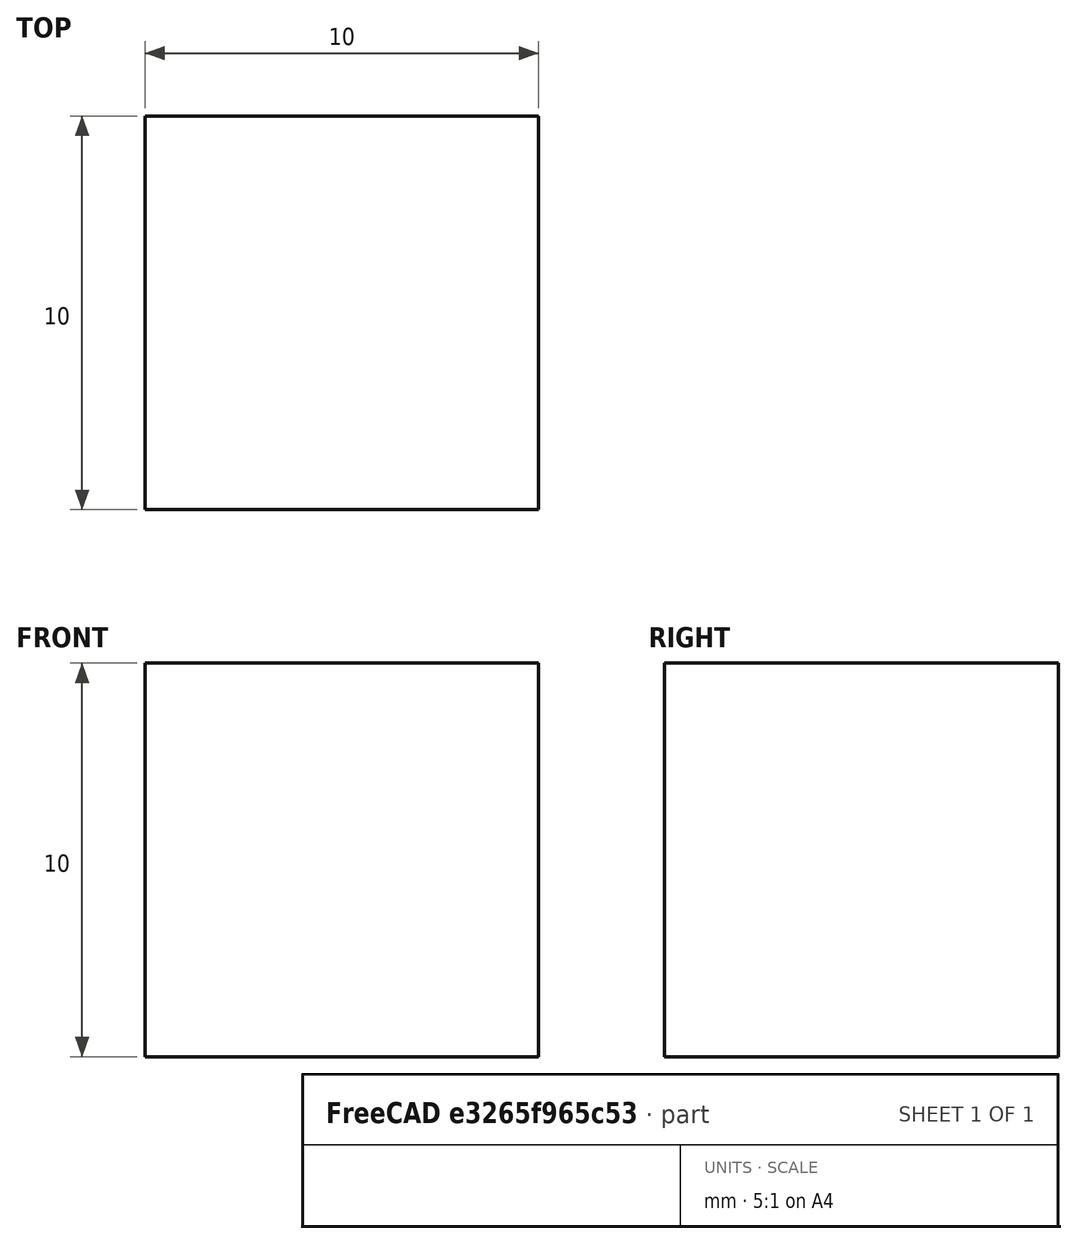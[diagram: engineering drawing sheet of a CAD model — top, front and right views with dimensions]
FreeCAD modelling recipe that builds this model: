
FCSTD DOCUMENT  (FreeCAD 1.0R39109 (Git))
Label: box
License: All rights reserved
LicenseURL: http://en.wikipedia.org/wiki/All_rights_reserved
objects: Part::Plane×4, Part::FeaturePython×1, Fem::ConstraintFixed×1, Fem::ConstraintForce×1, Fem::FemMeshShapeBaseObjectPython×1, Fem::FemSolverObjectPython×1, Fem::FeaturePython×1, App::MaterialObjectPython×1, Fem::FemMeshObjectPython×1, Fem::FemResultObjectPython×1, Fem::FemPostPipeline×1, App::TextDocument×1, Fem::FemAnalysis×1
note: 5 computed .brp shape members not serialized (recipe doc carries the construction recipe); baked Part::Feature solids carry a one-line shape summary decoded from their .brp

FEATURE [Part::Plane] Plane
  AttacherType = Attacher::AttachEngine3D
  Length = 10
  Placement = pos=(0,0,-10) rot=(0,0,1;0rad)
  Width = 10
FEATURE [Part::Plane] Plane001
  AttacherType = Attacher::AttachEngine3D
  Length = 10
  Placement = pos=(0,0,0) rot=(0,1,0;1.5708rad)
  Width = 10
FEATURE [Part::Plane] Plane002
  AttacherType = Attacher::AttachEngine3D
  Length = 10
  Placement = pos=(10,0,0) rot=(0,1,0;1.5708rad)
  Width = 10
FEATURE [Part::Plane] Plane003
  AttacherType = Attacher::AttachEngine3D
  Length = 10
  Width = 10
FEATURE [Part::FeaturePython] BooleanFragments  # WARN: FeaturePython — macro-defined, semantics opaque (R4)
  Mode = 0
  Objects = -> [Plane,Plane001,Plane002,Plane003]
  Tolerance = 0
FEATURE [Fem::ConstraintFixed] ConstraintFixed
  NormalDirection = (0,0,1)
  Normals = (4) [(0,0,1),(0,0,1),(0,0,1),(0,0,1)]
  Points = (4) [(0,0,-10),(0,10,-10),(10,0,-10),(10,10,-10)]
  References = -> [BooleanFragments]
  Suppressed = false
FEATURE [Fem::ConstraintForce] ConstraintForce
  Direction = -> BooleanFragments [Edge11]
  DirectionVector = (1,0,0)
  Force = 1000
  NormalDirection = (0,0,1)
  Normals = (2) [(0,0,1),(0,0,1)]
  Points = (2) [(0,0,0),(0,10,0)]
  References = -> [BooleanFragments]
  Suppressed = false
FEATURE [Fem::FemMeshShapeBaseObjectPython] FEMMeshGmsh  # FEM object (typed FeaturePython)
  Algorithm2D = 0
  Algorithm3D = 0
  CharacteristicLengthMax = 0
  CharacteristicLengthMin = 0
  CoherenceMesh = true
  ElementDimension = 2
  ElementOrder = 1
  GeometryTolerance = 1e-06
  GroupsOfNodes = false
  HighOrderOptimize = 0
  MeshSizeFromCurvature = 12
  OptimizeNetgen = false
  OptimizeStd = true
  RecombinationAlgorithm = 0
  Recombine3DAll = false
  RecombineAll = false
  SecondOrderLinear = false
  Shape = -> BooleanFragments
  SubdivisionAlgorithm = 0
FEATURE [Fem::FemSolverObjectPython] SolverCcxTools  # FEM object (typed FeaturePython)
  AnalysisType = 0
  BeamReducedIntegration = true
  BeamShellResultOutput3D = false
  BucklingFactors = 1
  EigenmodeHighLimit = 1000000
  EigenmodeLowLimit = 0
  EigenmodesCount = 10
  GeometricalNonlinearity = 0
  IterationsControlParameterCutb = 0.25,0.5,0.75,0.85,,,1.5,
  IterationsControlParameterIter = 4,8,9,200,10,400,,200,,
  IterationsControlParameterTimeUse = false
  IterationsMaximum = 2000
  IterationsUserDefinedIncrementations = false
  IterationsUserDefinedTimeStepLength = false
  MaterialNonlinearity = 0
  MatrixSolverType = 0
  ModelSpace = 0
  OutputFrequency = 1
  SplitInputWriter = false
  ThermoMechSteadyState = true
  ThermoMechType = 0
  TimeEnd = 1
  TimeInitialStep = 0.01
  TimeMaximumStep = 1
  TimeMinimumStep = 1e-05
FEATURE [Fem::FeaturePython] ElementGeometry2D  # FEM object (typed FeaturePython)
  Thickness = 1
FEATURE [App::MaterialObjectPython] MaterialSolid  # material (typed FeaturePython)
  Category = 0
  Material = AmbientColor=(0.0020, 0.0020, 0.0020, 1.0),Author=Juergen Riegel,AuthorAndLicense=CC-BY-3.0,CardName=CalculiX-Steel,Density=7.9e-06 kg/mm^3,+14 more (map truncated)
  UUID = 92589471-a6cb-4bbc-b748-d425a17dea7d
FEATURE [Fem::FemMeshObjectPython] CCX_Results_Mesh  # FEM object (typed FeaturePython)
FEATURE [Fem::FemResultObjectPython] CCX_Results  # FEM object (typed FeaturePython)
  DisplacementLengths = [0,0,0,0,0.000317151,0.000317149,0.00031497,0.000314968,0,0,0,0,0,0,0,0,0,0,0,2.94628e-09,3.02415e-09,3.00043e-09,3.02909e-09,2.95756e-09,3.97421e-09,3.19864e-09,3.05178e-09,3.05413e-09,3.20728e-09,3.98628e-09,0,0,0,0,0,0,0,0,0,0,0,+839 more]
  DisplacementVectors = (880) [(0,0,0),(0,0,0),(0,0,0),(0,0,0),(0.00031715,-8.45803e-07,3.88839e-07),(0.000317148,8.44059e-07,3.89458e-07),(0.000314969,4.78234e-07,-6.08826e-07),+873 more]
  Eigenmode = 0
  EigenmodeFrequency = 0
  MaxShear = [0.0548959,0.0548447,0.0544567,0.0544046,0.0746887,0.0747767,0.0625416,0.0625647,0.0440682,0.0337027,0.0362306,0.0337779,0.0440447,0.0182881,0.0370169,0.0377786,0.0379453,0.0370668,0.0182972,0.000184373,3.73367e-05,1.79001e-06,3.76396e-05,+857 more]
  Mesh = -> CCX_Results_Mesh
  NodeNumbers = [1,2,3,4,5,6,7,8,9,10,11,12,13,14,15,16,17,18,19,20,21,22,23,24,25,26,27,28,29,30,31,32,33,34,35,36,37,38,39,40,41,42,43,44,45,46,47,48,49,50,51,52,53,54,55,56,57,58,59,60,61,62,63,64,65,66,67,68,69,+811 more]
  NodeStrainXX = [-2.93483e-08,-2.93743e-08,2.93671e-08,2.93902e-08,-3.64062e-07,-3.64326e-07,1.67714e-07,1.67519e-07,-2.30956e-08,-2.23958e-08,-2.639e-08,-2.24236e-08,-2.31302e-08,-2.04316e-08,-1.74632e-08,-2.17632e-08,-2.18188e-08,-1.74988e-08,+862 more]
  NodeStrainXY = [-3.77972e-08,3.7876e-08,-3.76633e-08,3.77454e-08,1.46119e-07,-1.46048e-07,1.58126e-07,-1.58018e-07,-1.56336e-08,-1.47411e-08,-1.19399e-10,1.42119e-08,1.57255e-08,-3.05797e-08,-1.99003e-09,-1.67503e-08,1.65514e-08,1.988e-09,3.06329e-08,+861 more]
  NodeStrainXZ = [-3.28965e-07,-3.28617e-07,-3.26214e-07,-3.25861e-07,-1.93783e-07,-1.94471e-07,-1.91882e-07,-1.92055e-07,2.67141e-07,2.02304e-07,2.18259e-07,2.02819e-07,2.66978e-07,9.20066e-08,2.24644e-07,2.28393e-07,2.29457e-07,2.2495e-07,9.20384e-08,+861 more]
  NodeStrainYY = [-1.48238e-08,-1.48194e-08,1.46836e-08,1.46785e-08,3.32011e-07,3.32288e-07,-2.59411e-07,-2.59437e-07,5.98466e-10,2.66905e-11,-3.22278e-10,2.27532e-11,5.99342e-10,8.69394e-14,5.33533e-14,9.81687e-14,9.9542e-14,5.36697e-14,8.69007e-14,+861 more]
  NodeStrainYZ = [3.4744e-08,-3.47794e-08,-3.43382e-08,3.43731e-08,-1.74433e-07,1.74363e-07,1.60923e-07,-1.60994e-07,2.196e-08,1.08085e-08,-9.82232e-12,-1.08047e-08,-2.19582e-08,2.88637e-08,1.57787e-08,5.55385e-09,-5.55607e-09,-1.57829e-08,-2.88644e-08,+861 more]
  NodeStrainZZ = [1.12252e-07,1.12324e-07,-1.12152e-07,-1.12216e-07,-1.85121e-07,-1.85344e-07,2.12696e-07,2.12981e-07,7.22729e-08,7.19567e-08,7.68914e-08,7.19965e-08,7.23315e-08,7.60434e-08,6.7106e-08,7.18585e-08,7.18882e-08,6.71643e-08,7.60949e-08,+861 more]
  NodeStressXX = [0.00350727,0.00350917,-0.00350683,-0.0035087,-0.0851212,-0.0851893,0.0417518,0.0417281,0.00229968,0.00238994,0.00181638,0.00238643,0.00229711,0.0034371,0.00319343,0.00255365,0.00254155,0.00319045,0.00343942,-1.44183e-05,5.30419e-06,+859 more]
  NodeStressXY = [-0.0061057,0.00611843,-0.00608407,0.00609734,0.0236038,-0.0235924,0.0255433,-0.0255259,-0.00252542,-0.00238125,-1.92876e-05,0.00229577,0.00254027,-0.0049398,-0.000321466,-0.00270581,0.00267368,0.000321139,0.00494839,3.88318e-05,1.16268e-05,+859 more]
  NodeStressXZ = [-0.0531406,-0.0530843,-0.0526962,-0.0526391,-0.0313033,-0.0314146,-0.0309964,-0.0310242,0.0431536,0.0326799,0.0352572,0.032763,0.0431273,0.0148626,0.0362887,0.0368943,0.0370661,0.0363381,0.0148677,-1.79571e-18,-3.50672e-19,-5.57136e-19,+858 more]
  NodeStressYY = [0.00585353,0.00586036,-0.00587878,-0.0058852,0.0273213,0.0273407,-0.0272454,-0.0272418,0.00612719,0.00601204,0.00602733,0.00601238,0.00613035,0.00673761,0.00601442,0.00606926,0.00606613,0.00601718,0.00674216,4.36822e-05,1.5813e-05,+859 more]
  NodeStressYZ = [0.0056125,-0.0056182,-0.00554695,0.00555257,-0.0281777,0.0281663,0.0259953,-0.0260067,0.00354738,0.00174599,-1.58668e-06,-0.00174538,-0.00354709,0.0046626,0.00254887,0.00089716,-0.000897519,-0.00254955,-0.00466272,5.0822e-19,-4.74338e-19,+859 more]
  NodeStressZZ = [0.0263812,0.0263989,-0.0263676,-0.0263836,-0.0562153,-0.0562769,0.0490181,0.0490718,0.0177054,0.0176315,0.0185003,0.0176389,0.0177178,0.0190215,0.0168546,0.0176772,0.0176788,0.0168668,0.0190344,0.000334883,7.2473e-05,-8.15613e-08,+858 more]
  PrincipalMax = [0.0703451,0.0703054,0.03902,0.0389572,0.0440357,0.0440471,0.0766657,0.0767152,0.0538636,0.0435678,0.046389,0.0436516,0.0538435,0.0281131,0.0470253,0.0478014,0.0479648,0.0470798,0.0281271,0.000334883,7.2473e-05,1.90551e-06,2.7536e-06,+857 more]
  PrincipalMed = [0.00484352,0.00484696,-0.00487976,-0.00488274,-0.0527093,-0.0526663,0.0352762,0.0352572,0.00654142,0.00630337,0.00602733,0.00629016,0.00654756,0.00954637,0.00604563,0.00625436,0.00624733,0.00604829,0.0095562,6.31276e-05,2.33176e-05,+859 more]
  PrincipalMin = [-0.0394467,-0.039384,-0.0698934,-0.069852,-0.105342,-0.105506,-0.0484174,-0.0484143,-0.0342728,-0.0238376,-0.0260723,-0.0239041,-0.0342458,-0.00846322,-0.0270085,-0.0277557,-0.0279257,-0.0270537,-0.00846727,-3.38637e-05,-2.20037e-06,+859 more]
  ResultType = Fem::ResultMechanical
  Stats = [0,0.00031715,-8.45803e-07,8.44059e-07,-1.98402e-05,1.92006e-05,0,0.000317151,1.80137e-06,0.162968,-4.95798e-05,0.10312,-0.0632023,0.0518934,-0.155505,4.76917e-05,1.02597e-06,0.0938969,0,0,0,0,0,0,0,0]
  Time = 0
  vonMises = [0.0956722,0.0955849,0.0949107,0.0948219,0.131231,0.131362,0.110371,0.110402,0.0763977,0.0584834,0.0628891,0.0586146,0.0763569,0.0316772,0.0642375,0.0655428,0.0658313,0.0643238,0.0316928,0.000331083,6.57401e-05,3.10665e-06,6.62424e-05,+857 more]
FEATURE [Fem::FemPostPipeline] Pipeline_CCX_Results
  Mode = 2
FEATURE [App::TextDocument] ccx_dat_file
  Text = <blob: 7039 chars omitted>
FEATURE [Fem::FemAnalysis] Analysis
  Group = -> [ConstraintFixed,ConstraintForce,FEMMeshGmsh,SolverCcxTools,ElementGeometry2D,MaterialSolid,CCX_Results,Pipeline_CCX_Results,ccx_dat_file]
